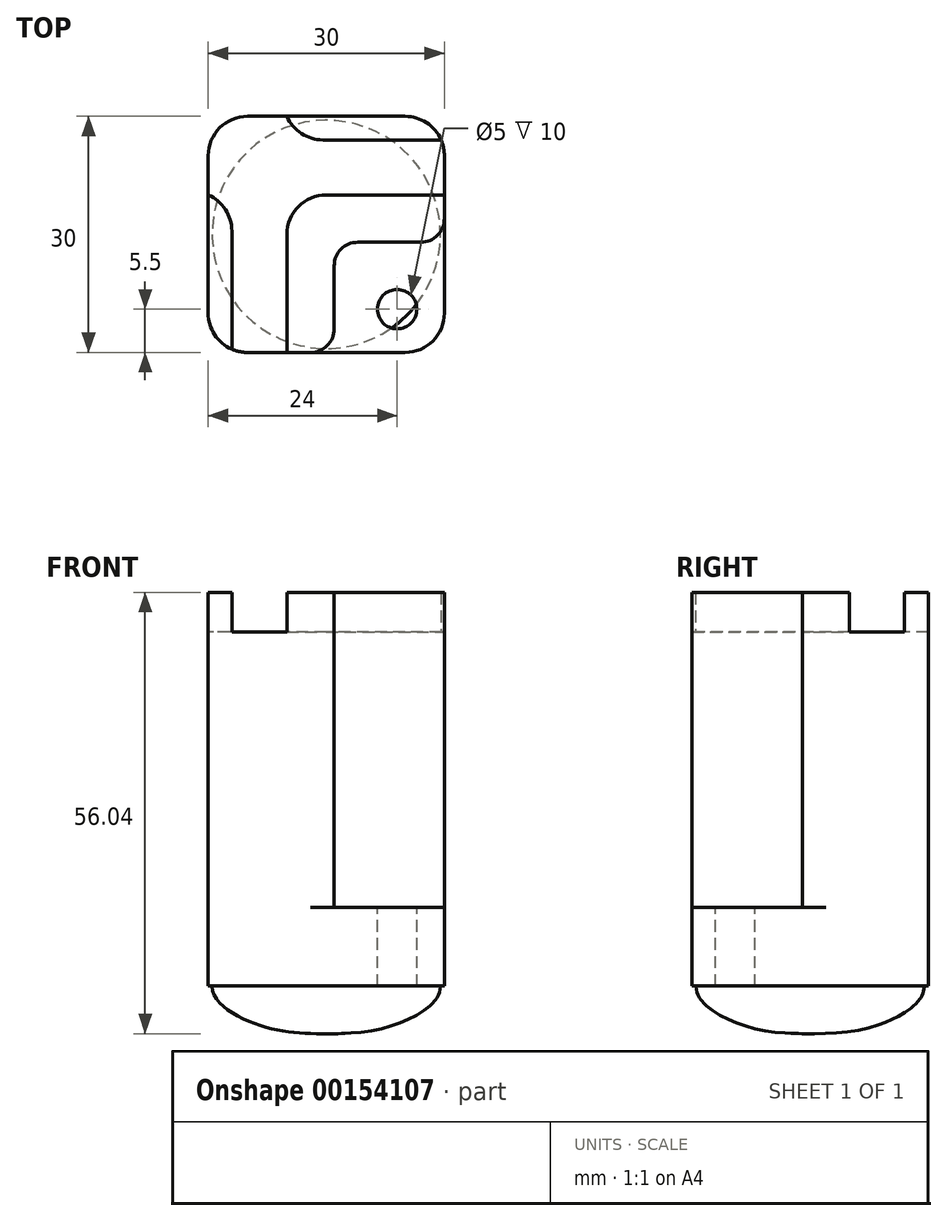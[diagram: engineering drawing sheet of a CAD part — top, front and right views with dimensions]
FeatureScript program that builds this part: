
annotation { "Feature Type Name" : "Feature", "Feature Type Description" : "" }
export const myFeature = defineFeature(function(context is Context, id is Id, definition is map)
    precondition{}
    {
        {
            var Q0;
            Q0=qCreatedBy(makeId("Top.planeOp"),FACE);
            var sketch = newSketch(context, id + "F0", { "sketchPlane" : qUnion([Q0])});
            skLineSegment(sketch, "E0.bottom", {"start": v(15, -15) * mm, "end": v(-15, -15) * mm});
            skLineSegment(sketch, "E0.top", {"start": v(15, 15) * mm, "end": v(-15, 15) * mm});
            skLineSegment(sketch, "E0.left", {"start": v(15, -15) * mm, "end": v(15, 15) * mm});
            skLineSegment(sketch, "E0.right", {"start": v(-15, -15) * mm, "end": v(-15, 15) * mm});
            skPoint(sketch, "E0.middle", {"position": v(0, 0) * mm});
            skSolve(sketch);
        }
        {
            var Q0;
            Q0 = qSketchRegion(id + "F0", true);
            extrude(context, id + "F1", {"entities" : qUnion([Q0]), "depth" : 10 * mm});
        }
        {
            var Q0;
            Q0=makeQuery(id+"F1.opExtrude","CAP_FACE",FACE,{"disambiguationData":[OSD([sQuery(id+"F0.wireOp",EDGE,"E0.bottom"),sQuery(id+"F0.wireOp",EDGE,"E0.top"),sQuery(id+"F0.wireOp",EDGE,"E0.left"),sQuery(id+"F0.wireOp",EDGE,"E0.right")])],"isStart":false});
            var sketch = newSketch(context, id + "F2", { "sketchPlane" : qUnion([Q0])});
            skLineSegment(sketch, "E1", {"start": v(-15, 15) * mm, "end": v(-15, -15) * mm});
            skLineSegment(sketch, "E2", {"start": v(-15, -15) * mm, "end": v(1, -15) * mm});
            skLineSegment(sketch, "E3", {"start": v(1, -15) * mm, "end": v(1, -1) * mm});
            skLineSegment(sketch, "E4", {"start": v(1, -1) * mm, "end": v(15, -1) * mm});
            skLineSegment(sketch, "E5", {"start": v(15, -1) * mm, "end": v(15, 15) * mm});
            skLineSegment(sketch, "E6", {"start": v(15, 15) * mm, "end": v(-15, 15) * mm});
            skSolve(sketch);
        }
        {
            var Q0;
            Q0 = qSketchRegion(id + "F2", true);
            extrude(context, id + "F3", {"entities" : qUnion([Q0]), "operationType" : NewBodyOperationType.ADD, "depth" : 40 * mm});
        }
        {
            var Q0;
            Q0=makeQuery(id+"F3.opExtrude","CAP_FACE",FACE,{"disambiguationData":[OSD([sQuery(id+"F2.wireOp",EDGE,"E1"),sQuery(id+"F2.wireOp",EDGE,"E2"),sQuery(id+"F2.wireOp",EDGE,"E3"),sQuery(id+"F2.wireOp",EDGE,"E4"),sQuery(id+"F2.wireOp",EDGE,"E5"),sQuery(id+"F2.wireOp",EDGE,"E6")])],"isStart":false});
            var sketch = newSketch(context, id + "F4", { "sketchPlane" : qUnion([Q0])});
            skLineSegment(sketch, "E7", {"start": v(-12, 15) * mm, "end": v(-12, -15) * mm});
            skLineSegment(sketch, "E8", {"start": v(-12, -15) * mm, "end": v(-5, -15) * mm});
            skLineSegment(sketch, "E9", {"start": v(-5, -15) * mm, "end": v(-5, 15) * mm});
            skLineSegment(sketch, "E10", {"start": v(-5, 15) * mm, "end": v(-12, 15) * mm});
            skLineSegment(sketch, "E11", {"start": v(-15, 5) * mm, "end": v(15, 5) * mm});
            skLineSegment(sketch, "E12", {"start": v(15, 5) * mm, "end": v(15, 12) * mm});
            skLineSegment(sketch, "E13", {"start": v(15, 12) * mm, "end": v(-15, 12) * mm});
            skLineSegment(sketch, "E14", {"start": v(-15, 12) * mm, "end": v(-15, 5) * mm});
            skLineSegment(sketch, "E15", {"start": v(-12, 15) * mm, "end": v(-15, 15) * mm});
            skLineSegment(sketch, "E16", {"start": v(-15, 15) * mm, "end": v(-15, 12) * mm});
            skSolve(sketch);
        }
        {
            var Q0;
            Q0 = qSketchRegion(id + "F4", true);
            extrude(context, id + "F5", {"entities" : qUnion([Q0]), "operationType" : NewBodyOperationType.REMOVE, "oppositeDirection" : true, "depth" : 5 * mm});
        }
        {
            var Q0;
            Q0=makeQuery(id+"F1.opExtrude","CAP_FACE",FACE,{"disambiguationData":[OSD([sQuery(id+"F0.wireOp",EDGE,"E0.bottom"),sQuery(id+"F0.wireOp",EDGE,"E0.top"),sQuery(id+"F0.wireOp",EDGE,"E0.left"),sQuery(id+"F0.wireOp",EDGE,"E0.right")])],"isStart":false});
            var sketch = newSketch(context, id + "F6", { "sketchPlane" : qUnion([Q0])});
            skCircle(sketch, "E17", {"center": v(9, -9.5) * mm, "radius": 2.5 * mm});
            skSolve(sketch);
        }
        {
            var Q0;
            Q0 = qSketchRegion(id + "F6", true);
            extrude(context, id + "F7", {"entities" : qUnion([Q0]), "operationType" : NewBodyOperationType.REMOVE, "endBound" : BoundingType.UP_TO_NEXT, "oppositeDirection" : true, "depth" : 25 * mm});
        }
        {
            var Q0;
            Q0=qCreatedBy(makeId("Front.planeOp"),FACE);
            var sketch = newSketch(context, id + "F8", { "sketchPlane" : qUnion([Q0])});
            skArc(sketch, "E18", {"start": v(-14.5, 0) * mm, "mid": v(-10.25, -10.25) * mm, "end": v(0, -14.5) * mm});
            skLineSegment(sketch, "E19", {"start": v(-14.5, 0) * mm, "end": v(0, 0) * mm});
            skLineSegment(sketch, "E20", {"start": v(0, 0) * mm, "end": v(0, -14.5) * mm});
            skFitSpline(sketch, "E21", {"points": [v(-14.5, 0) * mm, v(-8.93, -4.83) * mm, v(0, -6.04) * mm], "startDerivative": vector(-0.08, -13.28) * mm, "endDerivative": vector(17.17, 0.14) * mm});
            skSolve(sketch);
        }
        {
            var Q0;
            {var subQ1=sQuery(id+"F8.wireOp",EDGE,"E19");Q0=makeQuery(id+"F8.imprint","IMPRINT",FACE,{"disambiguationData":[TD([[makeQuery(id+"F8.imprint","IMPRINT",EDGE,{"derivedFrom":subQ1}),-1.0]])]});}
            var Q1;
            Q1=sQuery(id+"F8.wireOp",EDGE,"E18");
            var Q2;
            Q2=sQuery(id+"F8.wireOp",EDGE,"E20");
            revolve(context, id + "F9", {"operationType" : NewBodyOperationType.ADD, "entities" : qUnion([Q0]), "surfaceEntities" : qUnion([Q1]), "axis" : qUnion([Q2]), "revolveType" : RevolveType.FULL});
        }
        {
            var Q0;
            Q0=makeQuery(id+"F3.boolean.opBoolean","MERGE",EDGE,{"derivedFrom":[makeQuery(id+"F1.opExtrude","SWEPT_EDGE",EDGE,{"disambiguationData":[OSD([sQuery(id+"F0.wireOp",EDGE,"E0.bottom"),sQuery(id+"F0.wireOp",EDGE,"E0.right")])]}),makeQuery(id+"F3.opExtrude","SWEPT_EDGE",EDGE,{"disambiguationData":[OSD([sQuery(id+"F2.wireOp",EDGE,"E1"),sQuery(id+"F2.wireOp",EDGE,"E2")])]})]});
            var Q1;
            Q1=makeQuery(id+"F1.opExtrude","SWEPT_EDGE",EDGE,{"disambiguationData":[OSD([sQuery(id+"F0.wireOp",EDGE,"E0.bottom"),sQuery(id+"F0.wireOp",EDGE,"E0.left")])]});
            var Q2;
            Q2=makeQuery(id+"F3.boolean.opBoolean","MERGE",EDGE,{"derivedFrom":[makeQuery(id+"F1.opExtrude","SWEPT_EDGE",EDGE,{"disambiguationData":[OSD([sQuery(id+"F0.wireOp",EDGE,"E0.top"),sQuery(id+"F0.wireOp",EDGE,"E0.right")])]}),makeQuery(id+"F3.opExtrude","SWEPT_EDGE",EDGE,{"disambiguationData":[OSD([sQuery(id+"F2.wireOp",EDGE,"E1"),sQuery(id+"F2.wireOp",EDGE,"E6")])]})]});
            var Q3;
            Q3=makeQuery(id+"F3.boolean.opBoolean","MERGE",EDGE,{"derivedFrom":[makeQuery(id+"F1.opExtrude","SWEPT_EDGE",EDGE,{"disambiguationData":[OSD([sQuery(id+"F0.wireOp",EDGE,"E0.top"),sQuery(id+"F0.wireOp",EDGE,"E0.left")])]}),makeQuery(id+"F3.opExtrude","SWEPT_EDGE",EDGE,{"disambiguationData":[OSD([sQuery(id+"F2.wireOp",EDGE,"E5"),sQuery(id+"F2.wireOp",EDGE,"E6")])]})]});
            fillet(context, id + "F10", {"entities" : qUnion([Q0, Q1, Q2, Q3]), "radius" : 5 * mm, "tangentPropagation" : true, "allowEdgeOverflow" : false});
        }
        {
            var Q0;
            Q0=makeQuery(id+"F5.boolean.opBoolean","COPY",EDGE,{"derivedFrom":makeQuery(id+"F5.opExtrude","SWEPT_EDGE",EDGE,{"disambiguationData":[OSD([sQuery(id+"F4.wireOp",EDGE,"E9"),sQuery(id+"F4.wireOp",EDGE,"E11")])]})});
            var Q1;
            Q1=makeQuery(id+"F5.boolean.opBoolean","COPY",EDGE,{"derivedFrom":makeQuery(id+"F5.opExtrude","SWEPT_EDGE",EDGE,{"disambiguationData":[OSD([sQuery(id+"F4.wireOp",EDGE,"E9"),sQuery(id+"F4.wireOp",EDGE,"E13")])]})});
            var Q2;
            Q2=makeQuery(id+"F5.boolean.opBoolean","COPY",EDGE,{"derivedFrom":makeQuery(id+"F5.opExtrude","SWEPT_EDGE",EDGE,{"disambiguationData":[OSD([sQuery(id+"F4.wireOp",EDGE,"E7"),sQuery(id+"F4.wireOp",EDGE,"E11")])]})});
            fillet(context, id + "F11", {"entities" : qUnion([Q0, Q1, Q2]), "radius" : 5 * mm, "tangentPropagation" : true, "allowEdgeOverflow" : false});
        }
        {
            var Q0;
            Q0=makeQuery(id+"F3.opExtrude","SWEPT_EDGE",EDGE,{"disambiguationData":[OSD([sQuery(id+"F2.wireOp",EDGE,"E3"),sQuery(id+"F2.wireOp",EDGE,"E4")])]});
            var Q1;
            Q1=makeQuery(id+"F3.opExtrude","SWEPT_EDGE",EDGE,{"disambiguationData":[OSD([sQuery(id+"F0.wireOp",EDGE,"E0.bottom"),sQuery(id+"F2.wireOp",EDGE,"E2"),sQuery(id+"F2.wireOp",EDGE,"E3")])]});
            var Q2;
            Q2=makeQuery(id+"F3.opExtrude","SWEPT_EDGE",EDGE,{"disambiguationData":[OSD([sQuery(id+"F0.wireOp",EDGE,"E0.left"),sQuery(id+"F2.wireOp",EDGE,"E4"),sQuery(id+"F2.wireOp",EDGE,"E5")])]});
            fillet(context, id + "F12", {"entities" : qUnion([Q0, Q1, Q2]), "radius" : 3 * mm, "tangentPropagation" : true, "allowEdgeOverflow" : false});
        }
    });
